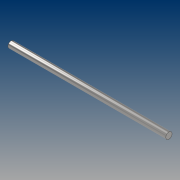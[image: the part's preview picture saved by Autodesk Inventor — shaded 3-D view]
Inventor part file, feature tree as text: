
AUTODESK INVENTOR PART (.ipt)
format: ipt  version: 2021 (Build 250183000, 183)  size: 75,264 bytes
history: native  units: mm
features: extrude x1, sketch x1
ambient origin geometry x8: Origin, YZ Plane, XZ Plane, XY Plane, X Axis, Y Axis, Z Axis, Center Point
bodies: Solid1 (feature_tree)
feature tree (2):
  extrude  "Extrusion1"  Depth=250.0mm TaperAngle=0.0deg
  sketch  "Sketch1"  dims[d0=10.0mm d1=250.0mm d2=0.0mm]
